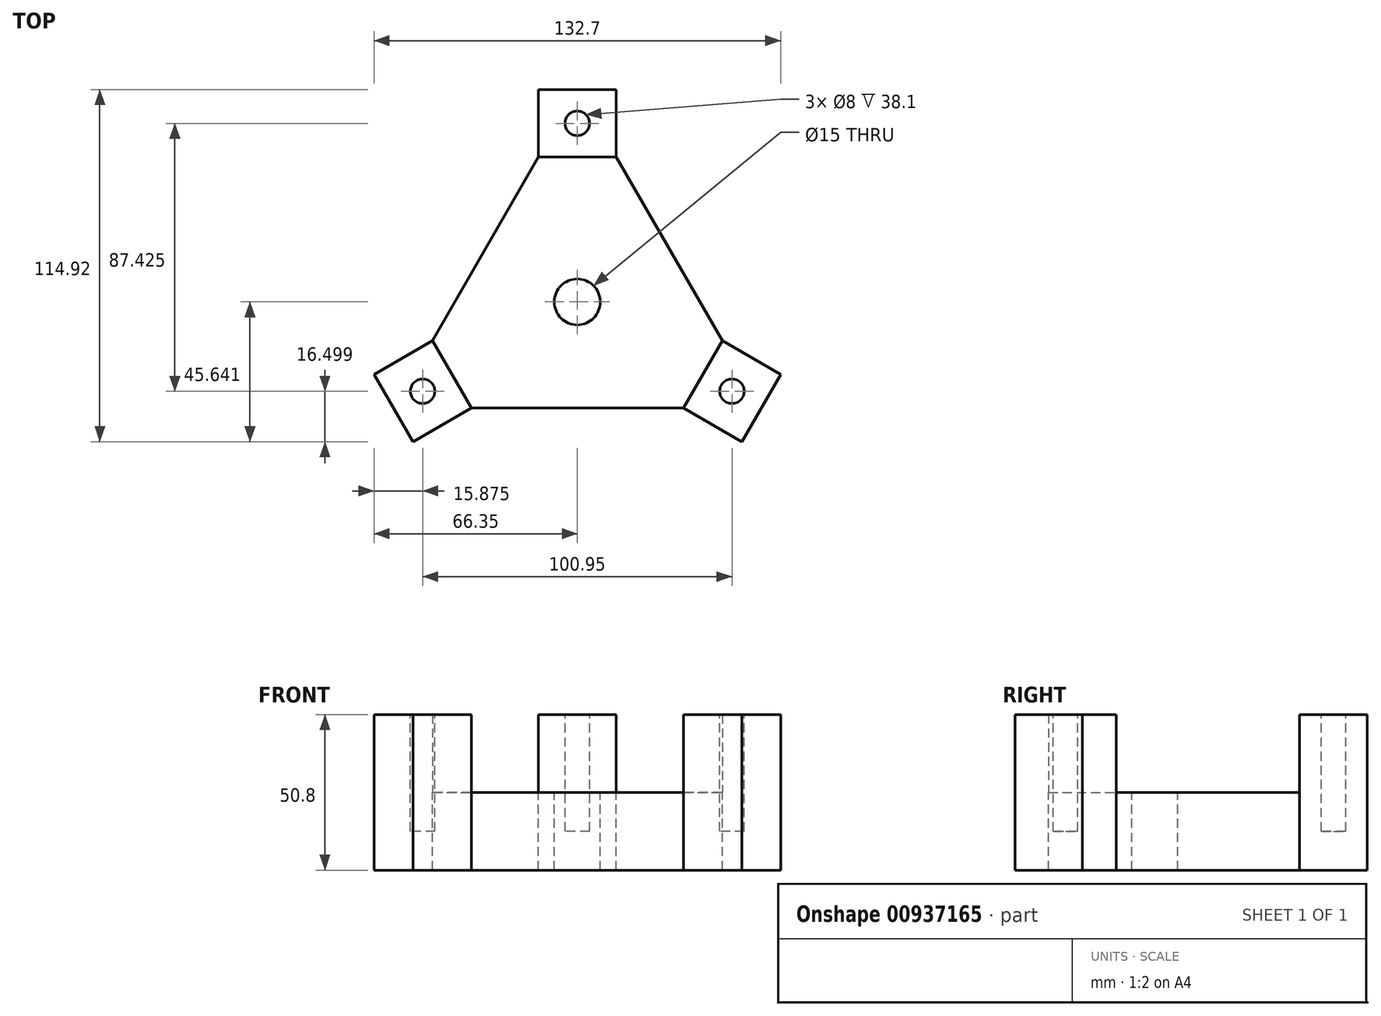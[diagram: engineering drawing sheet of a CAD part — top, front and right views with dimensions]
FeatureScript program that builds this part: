
annotation { "Feature Type Name" : "Feature", "Feature Type Description" : "" }
export const myFeature = defineFeature(function(context is Context, id is Id, definition is map)
    precondition{}
    {
        {
            var Q0;
            Q0=qCreatedBy(makeId("Top.planeOp"),FACE);
            var sketch = newSketch(context, id + "F0", { "sketchPlane" : qUnion([Q0])});
            skLineSegment(sketch, "E0", {"start": v(-60, 0) * mm, "end": v(0, 103.92) * mm});
            skLineSegment(sketch, "E1", {"start": v(60, 0) * mm, "end": v(0, 103.92) * mm});
            skLineSegment(sketch, "E2", {"start": v(-60, 0) * mm, "end": v(60, 0) * mm});
            skSolve(sketch);
        }
        {
            var Q0;
            Q0 = qSketchRegion(id + "F0", true);
            extrude(context, id + "F1", {"entities" : qUnion([Q0]), "depth" : 25.4 * mm, "offsetDistance" : 25.4 * mm});
        }
        {
            var Q0;
            Q0=makeQuery(id+"F1.opExtrude","CAP_FACE",FACE,{"disambiguationData":[OSD([sQuery(id+"F0.wireOp",EDGE,"E0"),sQuery(id+"F0.wireOp",EDGE,"E1"),sQuery(id+"F0.wireOp",EDGE,"E2")])],"isStart":false});
            var sketch = newSketch(context, id + "F2", { "sketchPlane" : qUnion([Q0])});
            skLineSegment(sketch, "E3", {"start": v(0, 103.92) * mm, "end": v(12.7, 103.92) * mm});
            skLineSegment(sketch, "E4", {"start": v(60, 0) * mm, "end": v(66.35, 11) * mm});
            skLineSegment(sketch, "E5", {"start": v(-60, 0) * mm, "end": v(-66.35, 11) * mm});
            skLineSegment(sketch, "E6", {"start": v(-60, 0) * mm, "end": v(-53.65, -11) * mm});
            skLineSegment(sketch, "E7", {"start": v(60, 0) * mm, "end": v(53.65, -11) * mm});
            skLineSegment(sketch, "E8", {"start": v(0, 103.92) * mm, "end": v(-12.7, 103.92) * mm});
            skLineSegment(sketch, "E9", {"start": v(-12.7, 103.92) * mm, "end": v(-12.7, 81.93) * mm});
            skLineSegment(sketch, "E10", {"start": v(12.7, 103.92) * mm, "end": v(12.7, 81.93) * mm});
            skLineSegment(sketch, "E11", {"start": v(53.65, -11) * mm, "end": v(34.6, 0) * mm});
            skLineSegment(sketch, "E12", {"start": v(66.35, 11) * mm, "end": v(47.3, 22) * mm});
            skLineSegment(sketch, "E13", {"start": v(-66.35, 11) * mm, "end": v(-47.3, 22) * mm});
            skLineSegment(sketch, "E14", {"start": v(-53.65, -11) * mm, "end": v(-34.6, 0) * mm});
            skLineSegment(sketch, "E15", {"start": v(-12.7, 81.93) * mm, "end": v(12.7, 81.93) * mm});
            skLineSegment(sketch, "E16", {"start": v(34.6, 0) * mm, "end": v(47.3, 22) * mm});
            skLineSegment(sketch, "E17", {"start": v(-34.6, 0) * mm, "end": v(-47.3, 22) * mm});
            skSolve(sketch);
        }
        {
            var Q0;
            {var subQ0=sQuery(id+"F2.wireOp",EDGE,"E3");Q0=makeQuery(id+"F2.imprint","IMPRINT",FACE,{"disambiguationData":[TD([[makeQuery(id+"F2.imprint","IMPRINT",EDGE,{"derivedFrom":subQ0}),-1.0]])]});}
            var Q1;
            {var subQ0=sQuery(id+"F2.wireOp",EDGE,"E4");Q1=makeQuery(id+"F2.imprint","IMPRINT",FACE,{"disambiguationData":[TD([[makeQuery(id+"F2.imprint","IMPRINT",EDGE,{"derivedFrom":subQ0}),1.0]])]});}
            var Q2;
            {var subQ0=sQuery(id+"F2.wireOp",EDGE,"E5");Q2=makeQuery(id+"F2.imprint","IMPRINT",FACE,{"disambiguationData":[TD([[makeQuery(id+"F2.imprint","IMPRINT",EDGE,{"derivedFrom":subQ0}),-1.0]])]});}
            var Q3;
            {var subQ0=sQuery(id+"F2.wireOp",EDGE,"E6");Q3=makeQuery(id+"F2.imprint","IMPRINT",FACE,{"disambiguationData":[TD([[makeQuery(id+"F2.imprint","IMPRINT",EDGE,{"derivedFrom":subQ0}),1.0]])]});}
            var Q4;
            {var subQ0=sQuery(id+"F2.wireOp",EDGE,"E15");Q4=makeQuery(id+"F2.imprint","IMPRINT",FACE,{"disambiguationData":[TD([[makeQuery(id+"F2.imprint","IMPRINT",EDGE,{"derivedFrom":subQ0}),1.0]])]});}
            var Q5;
            {var subQ0=sQuery(id+"F2.wireOp",EDGE,"E16");Q5=makeQuery(id+"F2.imprint","IMPRINT",FACE,{"disambiguationData":[TD([[makeQuery(id+"F2.imprint","IMPRINT",EDGE,{"derivedFrom":subQ0}),-1.0]])]});}
            var Q6;
            {var subQ0=sQuery(id+"F2.wireOp",EDGE,"E17");Q6=makeQuery(id+"F2.imprint","IMPRINT",FACE,{"disambiguationData":[TD([[makeQuery(id+"F2.imprint","IMPRINT",EDGE,{"derivedFrom":subQ0}),1.0]])]});}
            var Q7;
            {var subQ0=sQuery(id+"F2.wireOp",EDGE,"E7");Q7=makeQuery(id+"F2.imprint","IMPRINT",FACE,{"disambiguationData":[TD([[makeQuery(id+"F2.imprint","IMPRINT",EDGE,{"derivedFrom":subQ0}),-1.0]])]});}
            var Q8;
            {var subQ0=sQuery(id+"F2.wireOp",EDGE,"E8");Q8=makeQuery(id+"F2.imprint","IMPRINT",FACE,{"disambiguationData":[TD([[makeQuery(id+"F2.imprint","IMPRINT",EDGE,{"derivedFrom":subQ0}),1.0]])]});}
            extrude(context, id + "F3", {"entities" : qUnion([Q0, Q1, Q2, Q3, Q4, Q5, Q6, Q7, Q8]), "operationType" : NewBodyOperationType.ADD, "depth" : 25.4 * mm, "offsetDistance" : 25.4 * mm});
        }
        {
            var Q0;
            Q0 = qSketchRegion(id + "F2", true);
            extrude(context, id + "F4", {"entities" : qUnion([Q0]), "operationType" : NewBodyOperationType.ADD, "oppositeDirection" : true, "depth" : 25.4 * mm, "offsetDistance" : 25.4 * mm});
        }
        {
            var Q0;
            Q0=makeQuery(id+"F3.opExtrude","CAP_FACE",FACE,{"disambiguationData":[OSD([sQuery(id+"F2.wireOp",EDGE,"E4"),sQuery(id+"F2.wireOp",EDGE,"E7"),sQuery(id+"F2.wireOp",EDGE,"E11"),sQuery(id+"F2.wireOp",EDGE,"E12"),sQuery(id+"F2.wireOp",EDGE,"E16")])],"isStart":false});
            var sketch = newSketch(context, id + "F5", { "sketchPlane" : qUnion([Q0])});
            skCircle(sketch, "E18", {"center": v(0, 92.92) * mm, "radius": 4 * mm});
            skCircle(sketch, "E19", {"center": v(-50.48, 5.5) * mm, "radius": 4 * mm});
            skCircle(sketch, "E20", {"center": v(50.48, 5.5) * mm, "radius": 4 * mm});
            skSolve(sketch);
        }
        {
            var Q0;
            Q0 = qSketchRegion(id + "F5", true);
            extrude(context, id + "F6", {"entities" : qUnion([Q0]), "operationType" : NewBodyOperationType.REMOVE, "oppositeDirection" : true, "depth" : 38.1 * mm, "offsetDistance" : 25.4 * mm});
        }
        {
            var Q0;
            Q0=makeQuery(id+"F3.opExtrude","CAP_FACE",FACE,{"disambiguationData":[OSD([sQuery(id+"F2.wireOp",EDGE,"E4"),sQuery(id+"F2.wireOp",EDGE,"E7"),sQuery(id+"F2.wireOp",EDGE,"E11"),sQuery(id+"F2.wireOp",EDGE,"E12"),sQuery(id+"F2.wireOp",EDGE,"E16")])],"isStart":false});
            var sketch = newSketch(context, id + "F7", { "sketchPlane" : qUnion([Q0])});
            skCircle(sketch, "E21", {"center": v(0, 34.64) * mm, "radius": 7.5 * mm});
            skSolve(sketch);
        }
        {
            var Q0;
            Q0 = qSketchRegion(id + "F7", true);
            extrude(context, id + "F8", {"entities" : qUnion([Q0]), "operationType" : NewBodyOperationType.REMOVE, "oppositeDirection" : true, "depth" : 254 * mm, "offsetDistance" : 25.4 * mm});
        }
    });
